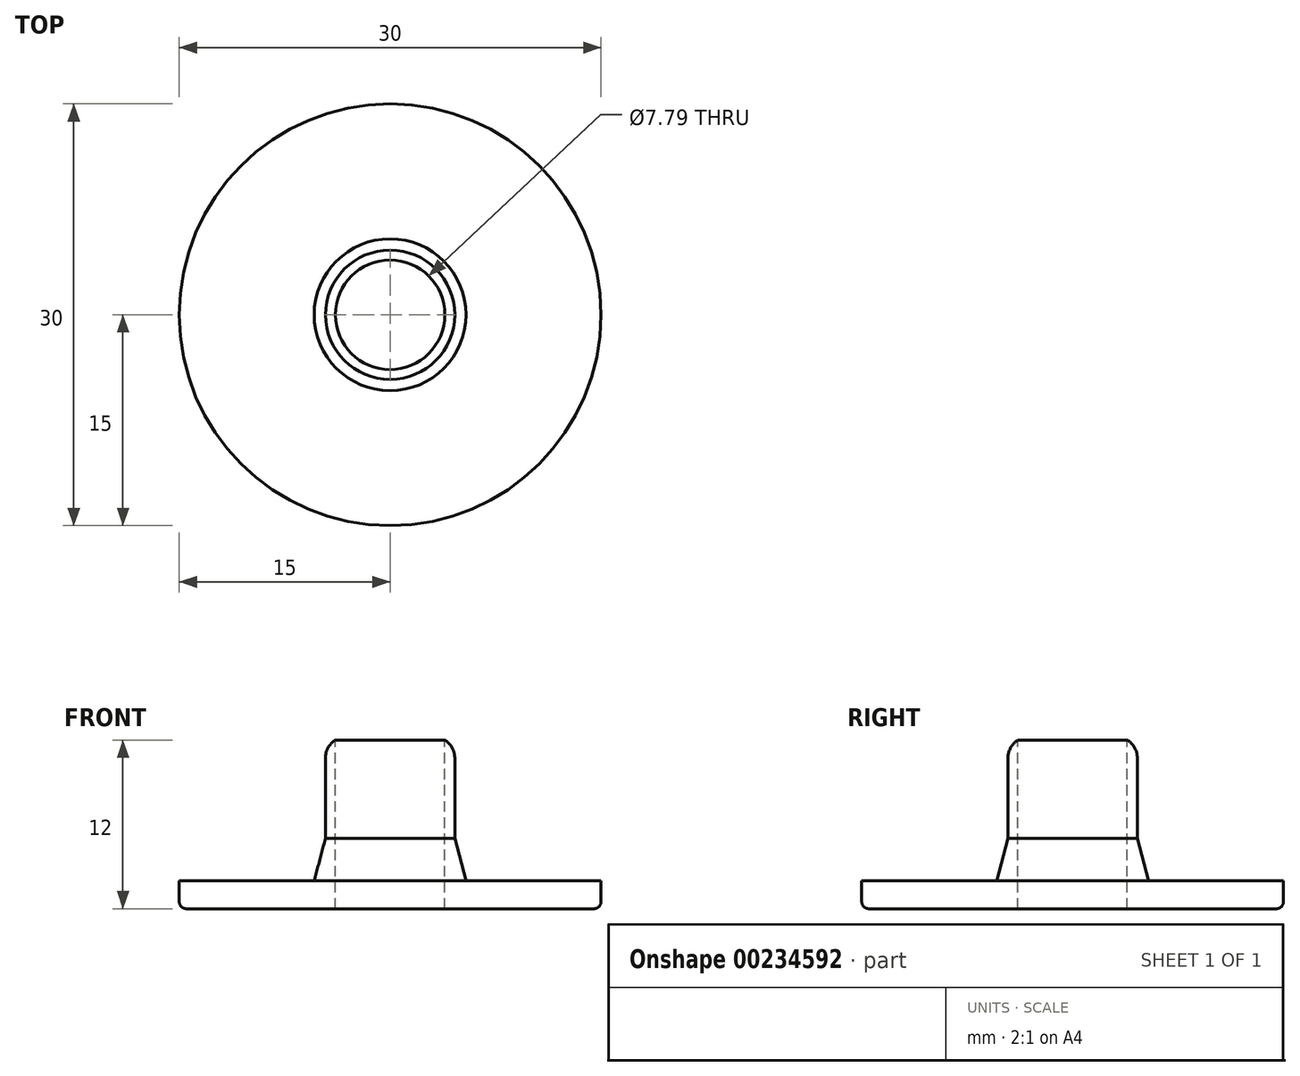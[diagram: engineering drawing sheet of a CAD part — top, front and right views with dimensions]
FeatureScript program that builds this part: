
annotation { "Feature Type Name" : "Feature", "Feature Type Description" : "" }
export const myFeature = defineFeature(function(context is Context, id is Id, definition is map)
    precondition{}
    {
        {
            var Q0;
            Q0=qCreatedBy(makeId("Front.planeOp"),FACE);
            var sketch = newSketch(context, id + "F0", { "sketchPlane" : qUnion([Q0])});
            skLineSegment(sketch, "E0", {"start": v(0, 0) * mm, "end": v(0, 12) * mm});
            skLineSegment(sketch, "E1", {"start": v(0, 12) * mm, "end": v(4.6, 12) * mm});
            skLineSegment(sketch, "E2", {"start": v(4.6, 12) * mm, "end": v(4.6, 5) * mm});
            skLineSegment(sketch, "E3", {"start": v(4.6, 5) * mm, "end": v(5.4, 2) * mm});
            skLineSegment(sketch, "E4", {"start": v(5.4, 2) * mm, "end": v(15, 2) * mm});
            skLineSegment(sketch, "E5", {"start": v(15, 2) * mm, "end": v(15, 0.5) * mm});
            skLineSegment(sketch, "E6", {"start": v(14.5, 0) * mm, "end": v(0, 0) * mm});
            skPoint(sketch, "E7.visualSharp", {"position": v(15, 2) * mm});
            skPoint(sketch, "E8.visualSharp", {"position": v(15, 0) * mm});
            skArc(sketch, "E8.filletArc", {"start": v(14.5, 0) * mm, "mid": v(14.85, 0.15) * mm, "end": v(15, 0.5) * mm});
            skSolve(sketch);
        }
        {
            var Q0;
            Q0 = qSketchRegion(id + "F0", true);
            var Q1;
            Q1=sQuery(id+"F0.wireOp",EDGE,"E0");
            revolve(context, id + "F1", {"entities" : qUnion([Q0]), "axis" : qUnion([Q1]), "revolveType" : RevolveType.FULL});
        }
        {
            var Q0;
            Q0=makeQuery(id+"F1.opRevolve","SWEPT_FACE",FACE,{"disambiguationData":[OSD([sQuery(id+"F0.wireOp",EDGE,"E6")])]});
            var sketch = newSketch(context, id + "F2", { "sketchPlane" : qUnion([Q0])});
            skLineSegment(sketch, "E9", {"start": v(-17.3, -6.92) * mm, "end": v(-6.9, 3.7) * mm});
            skLineSegment(sketch, "E10", {"start": v(-6.4, 3.98) * mm, "end": v(6.37, 6.88) * mm});
            skLineSegment(sketch, "E11", {"start": v(7.59, 5.97) * mm, "end": v(7.71, 3.96) * mm});
            skLineSegment(sketch, "E12", {"start": v(7.72, 3.86) * mm, "end": v(7.57, 0.69) * mm});
            skLineSegment(sketch, "E13", {"start": v(-17.02, -8.53) * mm, "end": v(-2.45, -15.44) * mm});
            skLineSegment(sketch, "E14", {"start": v(-1.36, -15.29) * mm, "end": v(3.19, -11.28) * mm});
            skArc(sketch, "E15", {"start": v(6.31, -0.23) * mm, "mid": v(0.3, -3.37) * mm, "end": v(2.94, -9.61) * mm});
            skPoint(sketch, "E16.visualSharp", {"position": v(-18.29, -7.92) * mm});
            skArc(sketch, "E16.filletArc", {"start": v(-17.3, -6.92) * mm, "mid": v(-17.58, -7.8) * mm, "end": v(-17.02, -8.53) * mm});
            skPoint(sketch, "E17.visualSharp", {"position": v(-6.7, 3.91) * mm});
            skArc(sketch, "E17.filletArc", {"start": v(-6.4, 3.98) * mm, "mid": v(-6.67, 3.87) * mm, "end": v(-6.9, 3.7) * mm});
            skPoint(sketch, "E18.visualSharp", {"position": v(7.5, 7.14) * mm});
            skArc(sketch, "E18.filletArc", {"start": v(7.59, 5.97) * mm, "mid": v(7.19, 6.7) * mm, "end": v(6.37, 6.88) * mm});
            skPoint(sketch, "E19.visualSharp", {"position": v(7.72, 3.91) * mm});
            skArc(sketch, "E19.filletArc", {"start": v(7.72, 3.86) * mm, "mid": v(7.72, 3.91) * mm, "end": v(7.71, 3.96) * mm});
            skPoint(sketch, "E20.visualSharp", {"position": v(7.5, -0.73) * mm});
            skArc(sketch, "E20.filletArc", {"start": v(6.31, -0.23) * mm, "mid": v(7.16, -0.08) * mm, "end": v(7.57, 0.69) * mm});
            skPoint(sketch, "E21.visualSharp", {"position": v(4.6, -10.04) * mm});
            skArc(sketch, "E21.filletArc", {"start": v(3.19, -11.28) * mm, "mid": v(3.52, -10.38) * mm, "end": v(2.94, -9.61) * mm});
            skPoint(sketch, "E22.visualSharp", {"position": v(-1.86, -15.72) * mm});
            skArc(sketch, "E22.filletArc", {"start": v(-2.45, -15.44) * mm, "mid": v(-1.88, -15.53) * mm, "end": v(-1.36, -15.29) * mm});
            skLineSegment(sketch, "E23", {"start": v(6.85, -0.23) * mm, "end": v(3.48, -10.83) * mm, "construction": true});
            skSolve(sketch);
        }
        {
            var Q0;
            Q0=makeQuery(id+"F1.opRevolve","SWEPT_FACE",FACE,{"disambiguationData":[OSD([sQuery(id+"F0.wireOp",EDGE,"E1")])]});
            var sketch = newSketch(context, id + "F3", { "sketchPlane" : qUnion([Q0])});
            skCircle(sketch, "E24", {"center": v(0, 0) * mm, "radius": 3.9 * mm});
            skSolve(sketch);
        }
        {
            var Q0;
            Q0 = qSketchRegion(id + "F3", true);
            extrude(context, id + "F4", {"entities" : qUnion([Q0]), "operationType" : NewBodyOperationType.REMOVE, "endBound" : BoundingType.THROUGH_ALL, "oppositeDirection" : true, "depth" : 25 * mm});
        }
        {
            var Q0;
            Q0=makeQuery(id+"F1.opRevolve","SWEPT_EDGE",EDGE,{"disambiguationData":[OSD([sQuery(id+"F0.wireOp",EDGE,"E1"),sQuery(id+"F0.wireOp",EDGE,"E2")])]});
            fillet(context, id + "F5", {"entities" : qUnion([Q0]), "radius" : 1.5 * mm, "tangentPropagation" : true, "allowEdgeOverflow" : false});
        }
    });
